# Revit family: okamura_MT20AA00_スプリント_スタンド_ボードスタンド_1200W×500D×1800H
name_source: partatom
category: 家具
revit_build: Autodesk Revit 2017 (Build: 20160225_1515(x64)
units: mm (PartAtom-declared; Revit-internal decimal feet)

## family parameters
OmniClass タイトル = General Furniture and Specialties
OmniClass 番号 = 23.40.20.00
ロード時にボイドで切り取り = いいえ
作業面に基づく = いいえ
共有 = いいえ
常に垂直 = はい
部屋計算ポイント = いいえ

## types (7) — shared parameters
D = 500  [stored 1.64042 ft]
H = 1800  [stored 5.90551 ft]
URL = http://www.okamura.co.jp
W = 1200  [stored 3.93701 ft]
アセンブリ コード = E2020200
キャスター = okm_G81
キーノート = 12490
区分 = スタンド
製品カテゴリ = クリエイティブファニチュア
製品コード/色仕様 = MT20AA
製造元 = 株式会社オカムラ

## per-type parameters (varying)
| type | 本体 |
| ZH11（オレンジレッド） | okm_ZH11 |
| ZH12（ダークグリーン） | okm_ZH12 |
| ZH13（イエロー） | okm_ZH13 |
| ZH14（セージ） | okm_ZH14 |
| ZH15（ダークグレー） | okm_ZH15 |
| Z721（ブラック） | okm_Z721 |
| ZC03（ネオホワイト） | okm_ZC03 |

note: [stored X ft] marks values corroborated as IEEE doubles in the binary element streams (Revit-internal decimal feet)
